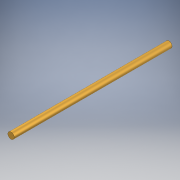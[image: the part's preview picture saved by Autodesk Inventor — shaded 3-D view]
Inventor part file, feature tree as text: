
AUTODESK INVENTOR PART (.ipt)
format: ipt  version: 2017 SP1 (Build 210196100, 196)  size: 91,648 bytes
history: native  units: in
note: dims shown in document units (in); Inventor stores cm internally (conversion verified against a paired STEP export)
features: extrude x1, sketch x1
ambient origin geometry x8: Origin, YZ Plane, XZ Plane, XY Plane, X Axis, Y Axis, Z Axis, Center Point
bodies: Solid1 (feature_tree)
feature tree (2):
  extrude  "Extrusion1"  Depth=2.9528in TaperAngle=0.0deg
  sketch  "Sketch1"  dims[d0=0.1181in d1=2.9528in d2=0.0in]
